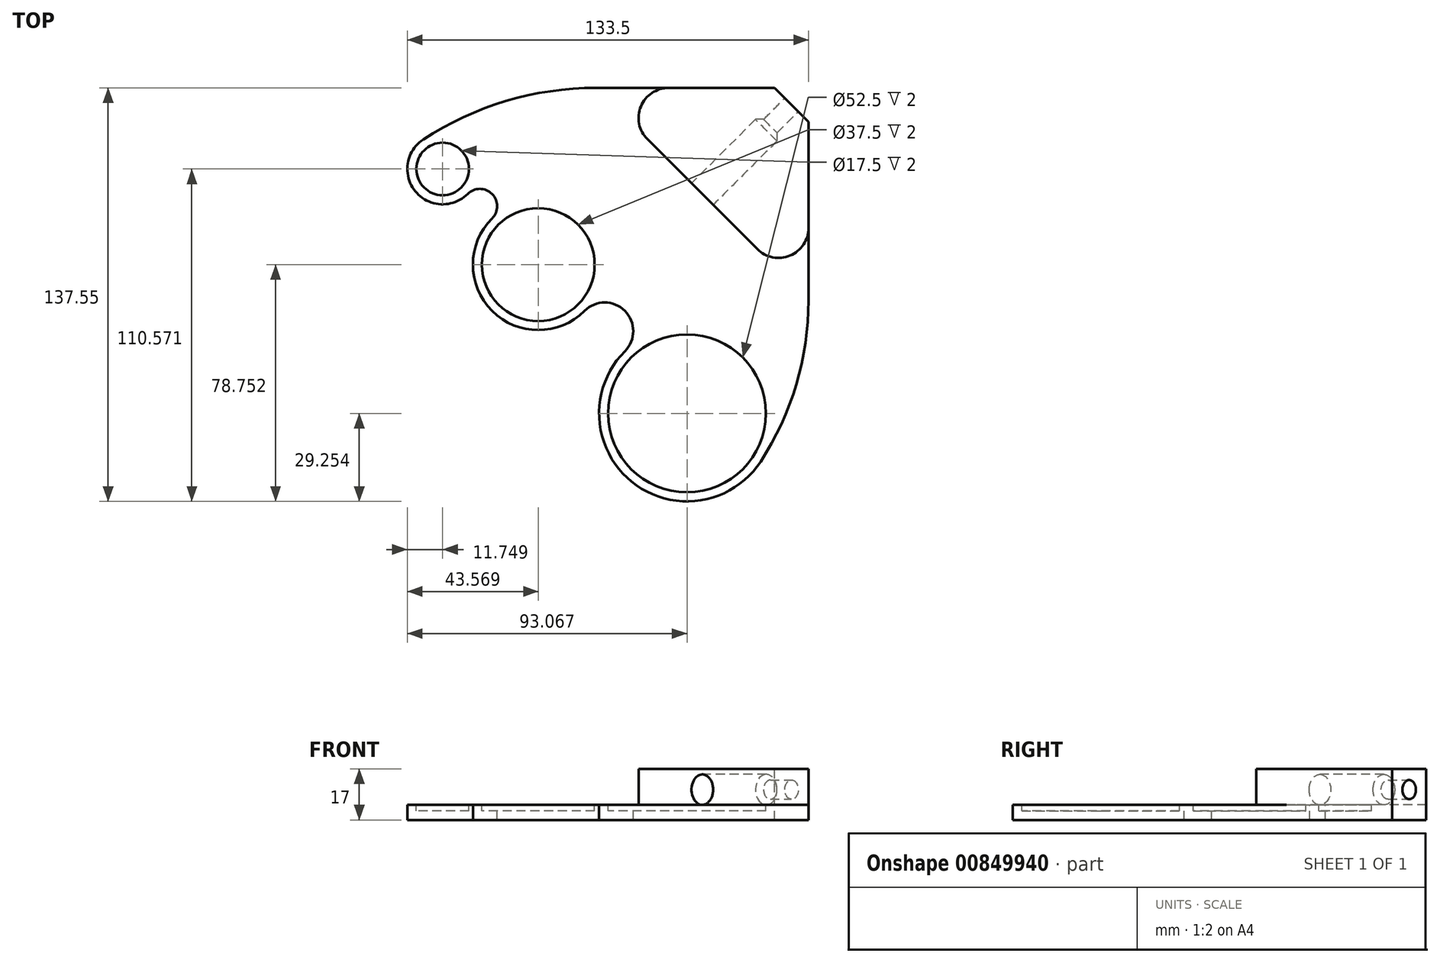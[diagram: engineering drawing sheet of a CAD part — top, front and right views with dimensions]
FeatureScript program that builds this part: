
annotation { "Feature Type Name" : "Feature", "Feature Type Description" : "" }
export const myFeature = defineFeature(function(context is Context, id is Id, definition is map)
    precondition{}
    {
        {
            var Q0;
            Q0=qCreatedBy(makeId("Top.planeOp"),FACE);
            var sketch = newSketch(context, id + "F0", { "sketchPlane" : qUnion([Q0])});
            skCircle(sketch, "E0", {"center": v(119.57, 51.7) * mm, "radius": 26.25 * mm, "construction": true});
            skCircle(sketch, "E1", {"center": v(70.07, 101.2) * mm, "radius": 18.75 * mm, "construction": true});
            skCircle(sketch, "E2", {"center": v(38.25, 133.02) * mm, "radius": 8.75 * mm, "construction": true});
            skLineSegment(sketch, "E3.bottom", {"start": v(0, 0) * mm, "end": v(160, 0) * mm, "construction": true});
            skLineSegment(sketch, "E3.left", {"start": v(0, 0) * mm, "end": v(0, 160) * mm, "construction": true});
            skLineSegment(sketch, "E3.right", {"start": v(160, 0) * mm, "end": v(160, 160) * mm, "construction": true});
            skLineSegment(sketch, "E4", {"start": v(119.57, 51.7) * mm, "end": v(101, 70.27) * mm, "construction": true});
            skLineSegment(sketch, "E5", {"start": v(101, 70.27) * mm, "end": v(83.33, 87.94) * mm, "construction": true});
            skLineSegment(sketch, "E6", {"start": v(83.33, 87.94) * mm, "end": v(70.07, 101.2) * mm, "construction": true});
            skLineSegment(sketch, "E7", {"start": v(70.07, 101.2) * mm, "end": v(56.81, 114.46) * mm, "construction": true});
            skLineSegment(sketch, "E8", {"start": v(56.81, 114.46) * mm, "end": v(44.44, 126.83) * mm, "construction": true});
            skLineSegment(sketch, "E9", {"start": v(44.44, 126.83) * mm, "end": v(38.25, 133.02) * mm, "construction": true});
            skArc(sketch, "E10", {"start": v(31.81, 142.85) * mm, "mid": v(29.13, 125.6) * mm, "end": v(46.56, 124.71) * mm});
            skArc(sketch, "E11", {"start": v(54.69, 116.58) * mm, "mid": v(54.69, 85.82) * mm, "end": v(85.45, 85.82) * mm});
            skArc(sketch, "E12", {"start": v(98.88, 72.39) * mm, "mid": v(101.13, 29) * mm, "end": v(144.06, 35.71) * mm});
            skArc(sketch, "E13", {"start": v(54.69, 116.58) * mm, "mid": v(54.69, 124.71) * mm, "end": v(46.56, 124.71) * mm});
            skArc(sketch, "E14", {"start": v(98.88, 72.39) * mm, "mid": v(98.88, 85.82) * mm, "end": v(85.45, 85.82) * mm});
            skLineSegment(sketch, "E15", {"start": v(0, 160) * mm, "end": v(160, 160) * mm, "construction": true});
            skCircle(sketch, "E16", {"center": v(119.57, 51.7) * mm, "radius": 38.25 * mm, "construction": true});
            skCircle(sketch, "E17", {"center": v(70.07, 101.2) * mm, "radius": 25 * mm, "construction": true});
            skCircle(sketch, "E18", {"center": v(38.25, 133.02) * mm, "radius": 13 * mm, "construction": true});
            skArc(sketch, "E19", {"start": v(89.29, 160) * mm, "mid": v(59.3, 155.62) * mm, "end": v(31.81, 142.85) * mm});
            skArc(sketch, "E20", {"start": v(144.06, 35.71) * mm, "mid": v(155.93, 61.34) * mm, "end": v(160, 89.29) * mm});
            skLineSegment(sketch, "E21", {"start": v(89.29, 160) * mm, "end": v(160, 89.29) * mm, "construction": true});
            skLineSegment(sketch, "E22", {"start": v(89.29, 160) * mm, "end": v(148.69, 160) * mm});
            skLineSegment(sketch, "E23", {"start": v(148.69, 160) * mm, "end": v(160, 148.69) * mm});
            skLineSegment(sketch, "E24", {"start": v(160, 148.69) * mm, "end": v(160, 89.29) * mm});
            skSolve(sketch);
        }
        {
            var Q0;
            Q0 = qSketchRegion(id + "F0", true);
            extrude(context, id + "F1", {"entities" : qUnion([Q0]), "oppositeDirection" : true, "depth" : 5 * mm, "offsetDistance" : 25 * mm});
        }
        {
            var Q0;
            Q0=qCreatedBy(makeId("Top.planeOp"),FACE);
            var sketch = newSketch(context, id + "F2", { "sketchPlane" : qUnion([Q0])});
            skCircle(sketch, "E25", {"center": v(38.25, 133.02) * mm, "radius": 8.75 * mm});
            skCircle(sketch, "E26", {"center": v(70.07, 101.2) * mm, "radius": 18.75 * mm});
            skCircle(sketch, "E27", {"center": v(119.57, 51.7) * mm, "radius": 26.25 * mm});
            skSolve(sketch);
        }
        {
            var Q0;
            Q0 = qSketchRegion(id + "F2", true);
            extrude(context, id + "F3", {"entities" : qUnion([Q0]), "operationType" : NewBodyOperationType.REMOVE, "oppositeDirection" : true, "depth" : 2 * mm, "offsetDistance" : 25 * mm});
        }
        {
            var Q0;
            Q0=qCreatedBy(makeId("Top.planeOp"),FACE);
            var sketch = newSketch(context, id + "F4", { "sketchPlane" : qUnion([Q0])});
            skLineSegment(sketch, "E28", {"start": v(148.69, 160) * mm, "end": v(160, 148.69) * mm});
            skLineSegment(sketch, "E29", {"start": v(160, 148.69) * mm, "end": v(160, 89.29) * mm});
            skLineSegment(sketch, "E30", {"start": v(160, 89.29) * mm, "end": v(89.29, 160) * mm});
            skLineSegment(sketch, "E31", {"start": v(89.29, 160) * mm, "end": v(148.69, 160) * mm});
            skSolve(sketch);
        }
        {
            var Q0;
            Q0 = qSketchRegion(id + "F4", true);
            extrude(context, id + "F5", {"entities" : qUnion([Q0]), "operationType" : NewBodyOperationType.ADD, "depth" : 12 * mm, "offsetDistance" : 25 * mm});
        }
        {
            var Q0;
            Q0=makeQuery(id+"F5.boolean.opBoolean","MERGE",FACE,{"derivedFrom":[makeQuery(id+"F1.opExtrude","SWEPT_FACE",FACE,{"disambiguationData":[OSD([sQuery(id+"F0.wireOp",EDGE,"E23")])]}),makeQuery(id+"F5.opExtrude","SWEPT_FACE",FACE,{"disambiguationData":[OSD([sQuery(id+"F4.wireOp",EDGE,"E28")])]})]});
            var sketch = newSketch(context, id + "F6", { "sketchPlane" : qUnion([Q0])});
            skCircle(sketch, "E32", {"center": v(0, 5.08) * mm, "radius": 5.08 * mm, "construction": true});
            skCircle(sketch, "E33", {"center": v(0, 5.08) * mm, "radius": 3.17 * mm});
            skSolve(sketch);
        }
        {
            var Q0;
            Q0 = qSketchRegion(id + "F6", true);
            extrude(context, id + "F7", {"entities" : qUnion([Q0]), "operationType" : NewBodyOperationType.REMOVE, "endBound" : BoundingType.THROUGH_ALL, "oppositeDirection" : true, "depth" : 25 * mm, "offsetDistance" : 25 * mm});
        }
        {
            var Q0;
            Q0=makeQuery(id+"F5.opExtrude","SWEPT_FACE",FACE,{"disambiguationData":[OSD([sQuery(id+"F4.wireOp",EDGE,"E30")])]});
            var sketch = newSketch(context, id + "F8", { "sketchPlane" : qUnion([Q0])});
            skCircle(sketch, "E34", {"center": v(0, 5.08) * mm, "radius": 5.08 * mm});
            skSolve(sketch);
        }
        {
            var Q0;
            Q0 = qSketchRegion(id + "F8", true);
            extrude(context, id + "F9", {"entities" : qUnion([Q0]), "operationType" : NewBodyOperationType.REMOVE, "oppositeDirection" : true, "depth" : 30 * mm, "offsetDistance" : 25 * mm});
        }
        {
            var Q0;
            Q0=makeQuery(id+"F9.boolean.opBoolean","INTERSECT",EDGE,{"derivedFrom":[makeQuery(id+"F7.boolean.opBoolean","COPY",FACE,{"derivedFrom":makeQuery(id+"F7.opExtrude","SWEPT_FACE",FACE,{"disambiguationData":[OSD([sQuery(id+"F6.wireOp",EDGE,"E33")])]})}),makeQuery(id+"F9.opExtrude","CAP_FACE",FACE,{"disambiguationData":[OSD([sQuery(id+"F8.wireOp",EDGE,"E34")])],"isStart":false})]});
            chamfer(context, id + "F10", {"entities" : qUnion([Q0]), "width" : 2 * mm, "tangentPropagation" : true});
        }
        {
            var Q0;
            Q0=makeQuery(id+"F5.opExtrude","SWEPT_EDGE",EDGE,{"disambiguationData":[OSD([sQuery(id+"F4.wireOp",EDGE,"E29"),sQuery(id+"F4.wireOp",EDGE,"E30")])]});
            var Q1;
            Q1=makeQuery(id+"F5.opExtrude","SWEPT_EDGE",EDGE,{"disambiguationData":[OSD([sQuery(id+"F4.wireOp",EDGE,"E30"),sQuery(id+"F4.wireOp",EDGE,"E31")])]});
            fillet(context, id + "F11", {"entities" : qUnion([Q0, Q1]), "radius" : 10 * mm, "tangentPropagation" : true, "allowEdgeOverflow" : false});
        }
    });
